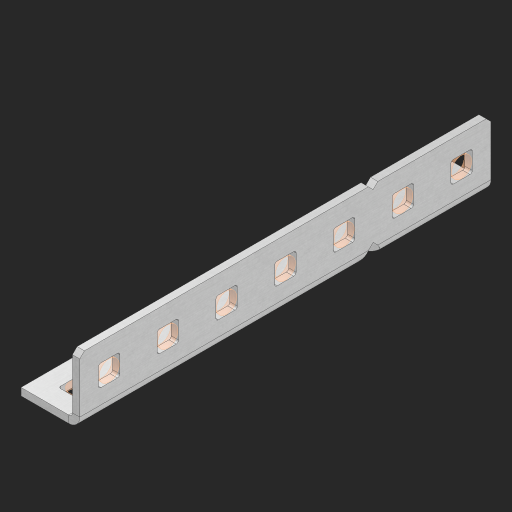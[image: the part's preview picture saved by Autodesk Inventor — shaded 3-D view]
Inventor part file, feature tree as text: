
AUTODESK INVENTOR PART (.ipt)
format: ipt  version: 2023 (Build 270158000, 158)  size: 529,920 bytes
history: native  units: in
note: dims shown in document units (in); Inventor stores cm internally (conversion verified against a paired STEP export)
features: other x19, extrude x13, sheet_metal_op x10, sketch x8, mirror x1, pattern_linear x1, chamfer x1
ambient origin geometry x8: Origin, YZ Plane, XZ Plane, XY Plane, X Axis, Y Axis, Z Axis, Center Point
bodies: Solid1 (feature_tree), Body (feature_tree)
feature tree (53):
  other  "Flange Pattern Plane"
  sheet_metal_op  "Flange Pattern"
  sheet_metal_op  "Body Pattern"
  other  "Arc Length"
  mirror  "Notch Mirror"
  pattern_linear  "Notch Pattern"  Spacing1=0.25in  [1 undecoded]
  chamfer  "End Chamfer"
  extrude  "Half Cut"  Depth=0.0625in
  sketch  "Sketch1"  dims[d0=1.5in]
  other  "Plate1"
  sketch  "Sketch2"  dims[d1=3.5in]
  other  "Plate2"
  sheet_metal_op  "Bend1"
  sheet_metal_op  "Corner1"
  sketch  "Sketch3"  dims[d2=0.0625in]
  other  "Flange Pattern Sketch"
  sketch  "Sketch7"  dims[d3=0.0625in]
  other  "Srf1"
  other  "Srf2"
  sketch  "Sketch8"  dims[d4=0.0312in]
  sketch  "Sketch9"  dims[d5=0.125in]
  other  "Srf91"
  sheet_metal_op  "Body Pattern Sketch"
  other  "Srf92"
  sketch  "Sketch13"  dims[d6=0.0625in]
  sketch  "Sketch14"  dims[d7=0.5in d8=90.0deg d9=0.0312in d10=0.25in d11=0.0625in d12=0.0625in d16=0.182in d17=0.02in d18=0.0625in d19=0.0in d20=0.25in d21=0.25in d46=0.172in d47=1.0in d48=0.0in d49=0.182in d50=0.02in d51=0.25in d52=0.25in d53=0.0625in d54=0.0in d55=0.172in d56=1.0in d57=0.0in d60=2.7559in d62=0.5in d63=0.3937in d65=0.5in d85=0.1473in d86=0.1782in d88=0.04in d89=0.0625in d90=0.0in d91=0.04in d92=0.0491in d95=2.5in d96=0.04in d97=0.25in d98=45.0deg d101=0.0in d102=2.497in d131=0.5in d132=2.7559in d134=0.5in d139=0.5in]
  other  "Srf856"
  other  "Srf1310"
  other  "Srf1311"
  other  "Srf1312"
  other  "Srf1376"
  other  "Srf1377"
  other  "Srf1728"
  other  "Srf1755"
  other  "Srf1878"
  other  "Srf1942"
  sheet_metal_op  "Flange Stamp"
  sheet_metal_op  "Flange Circle"
  sheet_metal_op  "Body Stamp"
  sheet_metal_op  "Body Circle"
  sheet_metal_op  "Notch"
  extrude  "ExtrusionSrf2"  Depth=0.0625in
  extrude  "ExtrusionSrf92"  Depth=0.5in
  extrude  "ExtrusionSrf856"  Depth=0.02in
  extrude  "ExtrusionSrf1310"  Depth=0.0625in
  extrude  "ExtrusionSrf1311"  TaperAngle=0.0deg  [1 undecoded]
  extrude  "ExtrusionSrf1312"  Depth=0.5in
  extrude  "ExtrusionSrf1376"  Depth=0.5in
  extrude  "ExtrusionSrf1377"  Depth=0.5in
  extrude  "ExtrusionSrf1728"  Depth=0.5in TaperAngle=0.0deg
  extrude  "ExtrusionSrf1755"  Depth=0.5in
  extrude  "ExtrusionSrf1878"  Depth=0.02in
  extrude  "ExtrusionSrf1942"  Depth=0.5in
note: 2 required parameter values undecoded (feature->parameter linkage not recoverable at this tier; creation-order binding heuristic only, values carry confidence <= 0.55)
